# Revit family: Domotics-DomesticRanges-GEWISS-SYSTEM_COMMAND-PUSH-BUTTON_KEY
name_source: partatom
category: Apparecchi elettrici
revit_build: Autodesk Revit 2016 (Build: 20161004_0715(x64)
units: mm (PartAtom-declared; Revit-internal decimal feet)

## family parameters
Condiviso = Sì
Host = Superficie
Mantenere orientamento annotazione = Sì
Numero OmniClass = 23.80.50.11.14
Punto di calcolo locali = Sì
Quota connettore circolare = Usa diametro
Taglio con vuoti quando caricato = Sì
Tipo di parte = Normale
Titolo OmniClass = Switches

## types (2) — shared parameters
Button key = With key
Carico apparente = 0 VA
Catalogue = DOMOTICS
Catalogue Range = SYSTEM - DOMESTIC RANGE
Description. = Push-button
Description: = 2P NO - 10A
Electrocod = 0130
IDF = 59407441-0af3-4d27-bd1c-ed09f17acc25
IDT = abcc67d3-aecf-43f9-b9cf-0a590a21eb3b
Immagine tipo = gw21530.jpg
N. poli = 1
No. SYSTEM modules = 1
Produttore = GEWISS S.p.A.
Prospetto di default = 1219 mm
Pulsante = GEWISS NERO
SEO = Push button
Simboli = SIMBOLO PULSANTI : PULSCHIAVE
Technical sheet = https://www.gewiss.com
Type = With key
URL = https://www.gewiss.com
Version file RFA = 19.4
Volt = 230 V
Voltage = 250 V ac
Voltage: = 250 V ac

## per-type parameters (varying)
| type | Colour | Descrizione | EAN code | Modello |
| GW20530 - Key-op.push-button-1P 10A NO white | White | KEY-OP.PUSH-BUTTON-1P 10A NO SY/WT | 8011564184640 | GW20530 |
| GW21530 - Key-op.push-button-1P 10A NO black | Black | KEY-OP.PUSH-BUTTON-1P 10A NA SY/BK | 8011564184657 | GW21530 |

## geometry (parser evidence)
native form markers: Sweep x1
no freeform markers — native parametric forms only
